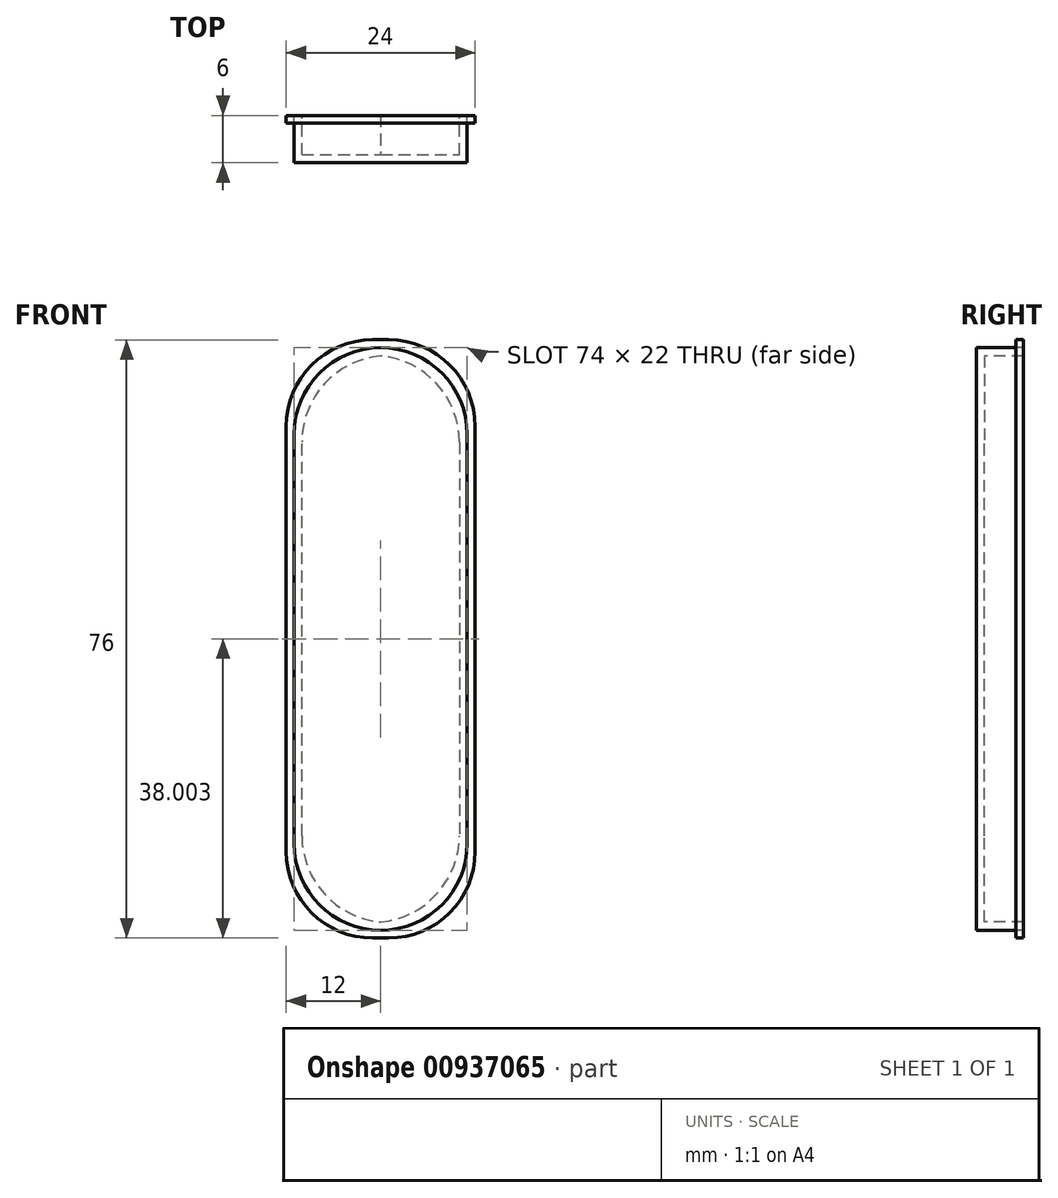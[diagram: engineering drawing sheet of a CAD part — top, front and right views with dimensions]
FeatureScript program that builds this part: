
annotation { "Feature Type Name" : "Feature", "Feature Type Description" : "" }
export const myFeature = defineFeature(function(context is Context, id is Id, definition is map)
    precondition{}
    {
        {
            var Q0;
            Q0=qCreatedBy(makeId("Front.planeOp"),FACE);
            var sketch = newSketch(context, id + "F0", { "sketchPlane" : qUnion([Q0])});
            skLineSegment(sketch, "E0.bottom", {"start": v(-1, 52.84) * mm, "end": v(21, 52.84) * mm});
            skLineSegment(sketch, "E0.top", {"start": v(-1, -21.16) * mm, "end": v(21, -21.16) * mm});
            skLineSegment(sketch, "E0.left", {"start": v(-1, 52.84) * mm, "end": v(-1, -21.16) * mm});
            skLineSegment(sketch, "E0.right", {"start": v(21, 52.84) * mm, "end": v(21, -21.16) * mm});
            skLineSegment(sketch, "E1", {"start": v(-2, 53.84) * mm, "end": v(22, 53.84) * mm});
            skLineSegment(sketch, "E2", {"start": v(22, 53.84) * mm, "end": v(22, -22.16) * mm});
            skLineSegment(sketch, "E3", {"start": v(22, -22.16) * mm, "end": v(-2, -22.16) * mm});
            skLineSegment(sketch, "E4", {"start": v(-2, 53.84) * mm, "end": v(-2, -22.16) * mm});
            skLineSegment(sketch, "E5", {"start": v(0, 51.84) * mm, "end": v(20, 51.84) * mm});
            skLineSegment(sketch, "E6", {"start": v(20, 51.84) * mm, "end": v(20, -20.16) * mm});
            skLineSegment(sketch, "E7", {"start": v(20, -20.16) * mm, "end": v(0, -20.16) * mm});
            skLineSegment(sketch, "E8", {"start": v(0, -20.16) * mm, "end": v(0, 51.84) * mm});
            skSolve(sketch);
        }
        {
            var Q0;
            Q0=makeQuery(id+"F0.imprint","IMPRINT",FACE,{"disambiguationData":[TD([[makeQuery(id+"F0.imprint","IMPRINT",EDGE,{"derivedFrom":sQuery(id+"F0.wireOp",EDGE,"E0.bottom")}),-1.0]])]});
            var Q1;
            Q1=makeQuery(id+"F0.imprint","IMPRINT",FACE,{"disambiguationData":[TD([[makeQuery(id+"F0.imprint","IMPRINT",EDGE,{"derivedFrom":sQuery(id+"F0.wireOp",EDGE,"E5")}),-1.0]])]});
            extrude(context, id + "F1", {"entities" : qUnion([Q0, Q1]), "depth" : 6 * mm, "offsetDistance" : 25 * mm});
        }
        {
            var Q0;
            Q0 = qSketchRegion(id + "F0", true);
            extrude(context, id + "F2", {"entities" : qUnion([Q0]), "depth" : 1 * mm, "offsetDistance" : 25 * mm});
        }
        {
            var Q0;
            Q0=makeQuery(id+"F0.imprint","IMPRINT",FACE,{"disambiguationData":[TD([[makeQuery(id+"F0.imprint","IMPRINT",EDGE,{"derivedFrom":sQuery(id+"F0.wireOp",EDGE,"E5")}),-1.0]])]});
            extrude(context, id + "F3", {"entities" : qUnion([Q0]), "operationType" : NewBodyOperationType.REMOVE, "depth" : 5 * mm, "offsetDistance" : 25 * mm});
        }
        {
            var Q0;
            Q0=makeQuery(id+"F2.opExtrude","SWEPT_EDGE",EDGE,{"disambiguationData":[OSD([sQuery(id+"F0.wireOp",EDGE,"E1"),sQuery(id+"F0.wireOp",EDGE,"E2")])]});
            var Q1;
            Q1=makeQuery(id+"F3.boolean.opBoolean","COPY",EDGE,{"derivedFrom":makeQuery(id+"F3.opExtrude","SWEPT_EDGE",EDGE,{"disambiguationData":[OSD([sQuery(id+"F0.wireOp",EDGE,"E5"),sQuery(id+"F0.wireOp",EDGE,"E6")])]})});
            var Q2;
            Q2=makeQuery(id+"F1.opExtrude","SWEPT_EDGE",EDGE,{"disambiguationData":[OSD([sQuery(id+"F0.wireOp",EDGE,"E0.bottom"),sQuery(id+"F0.wireOp",EDGE,"E0.right")])]});
            var Q3;
            Q3=makeQuery(id+"F2.opExtrude","SWEPT_EDGE",EDGE,{"disambiguationData":[OSD([sQuery(id+"F0.wireOp",EDGE,"E0.bottom"),sQuery(id+"F0.wireOp",EDGE,"E0.right")])]});
            var Q4;
            Q4=makeQuery(id+"F2.opExtrude","SWEPT_EDGE",EDGE,{"disambiguationData":[OSD([sQuery(id+"F0.wireOp",EDGE,"E1"),sQuery(id+"F0.wireOp",EDGE,"E4")])]});
            var Q5;
            Q5=makeQuery(id+"F1.opExtrude","SWEPT_EDGE",EDGE,{"disambiguationData":[OSD([sQuery(id+"F0.wireOp",EDGE,"E0.bottom"),sQuery(id+"F0.wireOp",EDGE,"E0.left")])]});
            var Q6;
            Q6=makeQuery(id+"F3.boolean.opBoolean","COPY",EDGE,{"derivedFrom":makeQuery(id+"F3.opExtrude","SWEPT_EDGE",EDGE,{"disambiguationData":[OSD([sQuery(id+"F0.wireOp",EDGE,"E5"),sQuery(id+"F0.wireOp",EDGE,"E8")])]})});
            var Q7;
            Q7=makeQuery(id+"F2.opExtrude","SWEPT_EDGE",EDGE,{"disambiguationData":[OSD([sQuery(id+"F0.wireOp",EDGE,"E0.bottom"),sQuery(id+"F0.wireOp",EDGE,"E0.left")])]});
            var Q8;
            Q8=makeQuery(id+"F2.opExtrude","SWEPT_EDGE",EDGE,{"disambiguationData":[OSD([sQuery(id+"F0.wireOp",EDGE,"E3"),sQuery(id+"F0.wireOp",EDGE,"E4")])]});
            var Q9;
            Q9=makeQuery(id+"F3.boolean.opBoolean","COPY",EDGE,{"derivedFrom":makeQuery(id+"F3.opExtrude","SWEPT_EDGE",EDGE,{"disambiguationData":[OSD([sQuery(id+"F0.wireOp",EDGE,"E7"),sQuery(id+"F0.wireOp",EDGE,"E8")])]})});
            var Q10;
            Q10=makeQuery(id+"F1.opExtrude","SWEPT_EDGE",EDGE,{"disambiguationData":[OSD([sQuery(id+"F0.wireOp",EDGE,"E0.top"),sQuery(id+"F0.wireOp",EDGE,"E0.left")])]});
            var Q11;
            Q11=makeQuery(id+"F2.opExtrude","SWEPT_EDGE",EDGE,{"disambiguationData":[OSD([sQuery(id+"F0.wireOp",EDGE,"E0.top"),sQuery(id+"F0.wireOp",EDGE,"E0.left")])]});
            var Q12;
            Q12=makeQuery(id+"F2.opExtrude","SWEPT_EDGE",EDGE,{"disambiguationData":[OSD([sQuery(id+"F0.wireOp",EDGE,"E2"),sQuery(id+"F0.wireOp",EDGE,"E3")])]});
            var Q13;
            Q13=makeQuery(id+"F3.boolean.opBoolean","COPY",EDGE,{"derivedFrom":makeQuery(id+"F3.opExtrude","SWEPT_EDGE",EDGE,{"disambiguationData":[OSD([sQuery(id+"F0.wireOp",EDGE,"E6"),sQuery(id+"F0.wireOp",EDGE,"E7")])]})});
            var Q14;
            Q14=makeQuery(id+"F1.opExtrude","SWEPT_EDGE",EDGE,{"disambiguationData":[OSD([sQuery(id+"F0.wireOp",EDGE,"E0.top"),sQuery(id+"F0.wireOp",EDGE,"E0.right")])]});
            var Q15;
            Q15=makeQuery(id+"F2.opExtrude","SWEPT_EDGE",EDGE,{"disambiguationData":[OSD([sQuery(id+"F0.wireOp",EDGE,"E0.top"),sQuery(id+"F0.wireOp",EDGE,"E0.right")])]});
            fillet(context, id + "F4", {"entities" : qUnion([Q0, Q1, Q2, Q3, Q4, Q5, Q6, Q7, Q8, Q9, Q10, Q11, Q12, Q13, Q14, Q15]), "radius" : 11 * mm, "tangentPropagation" : true, "allowEdgeOverflow" : false});
        }
    });
